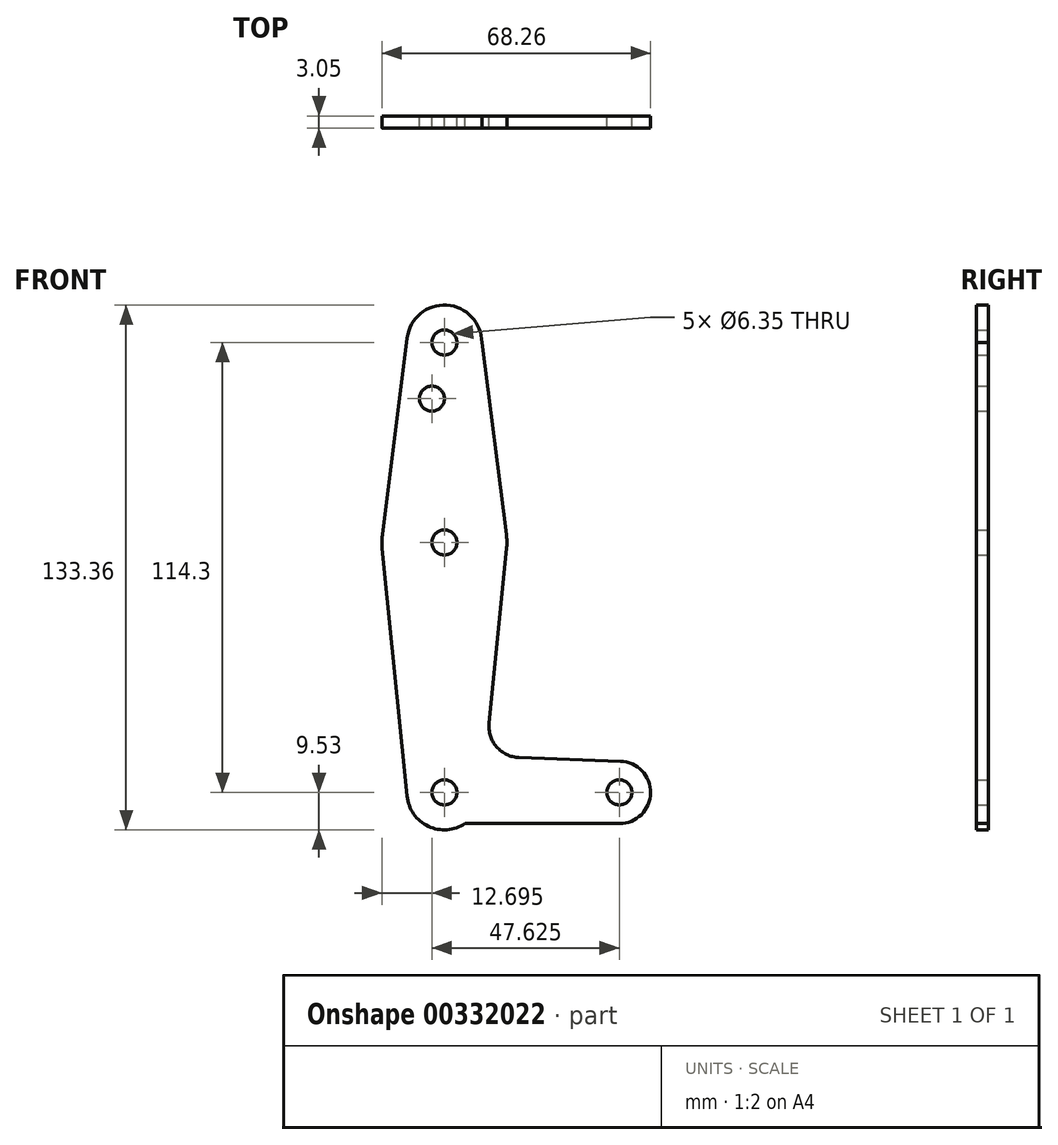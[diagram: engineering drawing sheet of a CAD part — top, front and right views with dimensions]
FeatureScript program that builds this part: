
annotation { "Feature Type Name" : "Feature", "Feature Type Description" : "" }
export const myFeature = defineFeature(function(context is Context, id is Id, definition is map)
    precondition{}
    {
        {
            var Q0;
            Q0=qCreatedBy(makeId("Front.planeOp"),FACE);
            var sketch = newSketch(context, id + "F0", { "sketchPlane" : qUnion([Q0])});
            skLineSegment(sketch, "E0", {"start": v(0, 0) * mm, "end": v(0, 114.3) * mm, "construction": true});
            skLineSegment(sketch, "E1", {"start": v(0, 0) * mm, "end": v(44.45, 0) * mm, "construction": true});
            skCircle(sketch, "E2", {"center": v(0, 114.3) * mm, "radius": 9.53 * mm});
            skCircle(sketch, "E3", {"center": v(0, 0) * mm, "radius": 9.53 * mm});
            skCircle(sketch, "E4", {"center": v(44.45, 0) * mm, "radius": 7.94 * mm});
            skCircle(sketch, "E5", {"center": v(0, 63.5) * mm, "radius": 15.88 * mm});
            skLineSegment(sketch, "E6", {"start": v(9.52, 114.3) * mm, "end": v(15.75, 65.5) * mm});
            skLineSegment(sketch, "E7", {"start": v(-9.45, 115.5) * mm, "end": v(-15.75, 65.48) * mm});
            skLineSegment(sketch, "E8", {"start": v(-15.8, 61.91) * mm, "end": v(-9.48, -0.95) * mm});
            skLineSegment(sketch, "E9", {"start": v(15.8, 61.91) * mm, "end": v(11.34, 17.6) * mm});
            skLineSegment(sketch, "E10", {"start": v(18.97, 8.85) * mm, "end": v(44.73, 7.93) * mm});
            skLineSegment(sketch, "E11", {"start": v(44.45, -7.94) * mm, "end": v(5.27, -7.94) * mm});
            skCircle(sketch, "E12", {"center": v(0, 0) * mm, "radius": 3.18 * mm});
            skCircle(sketch, "E13", {"center": v(44.45, 0) * mm, "radius": 3.18 * mm});
            skCircle(sketch, "E14", {"center": v(0, 63.5) * mm, "radius": 3.18 * mm});
            skCircle(sketch, "E15", {"center": v(0, 114.3) * mm, "radius": 3.18 * mm});
            skArc(sketch, "E16.filletArc", {"start": v(11.34, 17.6) * mm, "mid": v(13.26, 11.57) * mm, "end": v(18.97, 8.85) * mm});
            skCircle(sketch, "E17", {"center": v(-3.18, 100.03) * mm, "radius": 3.18 * mm});
            skSolve(sketch);
        }
        {
            var Q0;
            Q0 = qSketchRegion(id + "F0", true);
            extrude(context, id + "F1", {"entities" : qUnion([Q0]), "depth" : 3.05 * mm});
        }
    });
